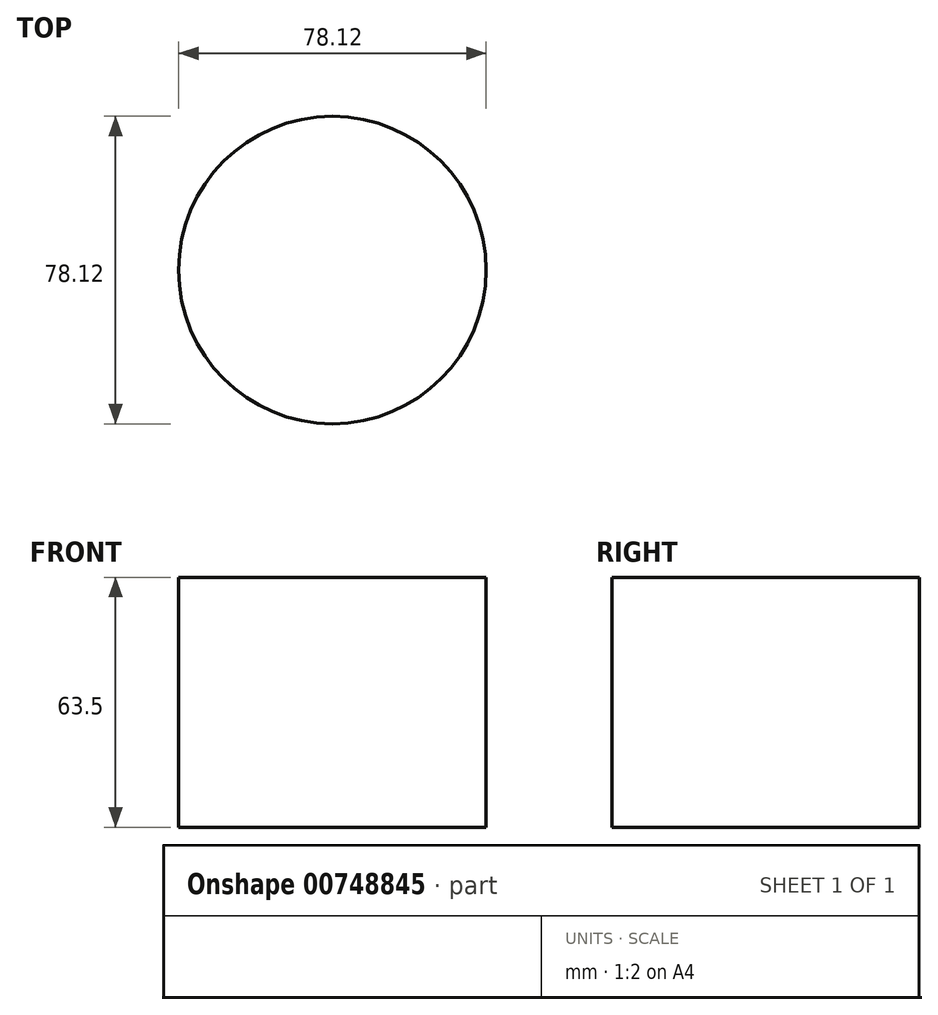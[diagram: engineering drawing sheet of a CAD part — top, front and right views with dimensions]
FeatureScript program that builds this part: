
annotation { "Feature Type Name" : "Feature", "Feature Type Description" : "" }
export const myFeature = defineFeature(function(context is Context, id is Id, definition is map)
    precondition{}
    {
        {
            var Q0;
            Q0=qCreatedBy(makeId("Top.planeOp"),FACE);
            var sketch = newSketch(context, id + "F0", { "sketchPlane" : qUnion([Q0])});
            skCircle(sketch, "E0", {"center": v(0, 0) * mm, "radius": 39.06 * mm});
            skSolve(sketch);
        }
        {
            var Q0;
            Q0=makeQuery(id+"F0.imprint","IMPRINT",FACE,{"disambiguationData":[TD([[makeQuery(id+"F0.imprint","IMPRINT",EDGE,{"derivedFrom":sQuery(id+"F0.wireOp",EDGE,"E0")}),1.0]])]});
            extrude(context, id + "F1", {"entities" : qUnion([Q0]), "oppositeDirection" : true, "depth" : 63.5 * mm, "offsetDistance" : 25.4 * mm});
        }
    });
